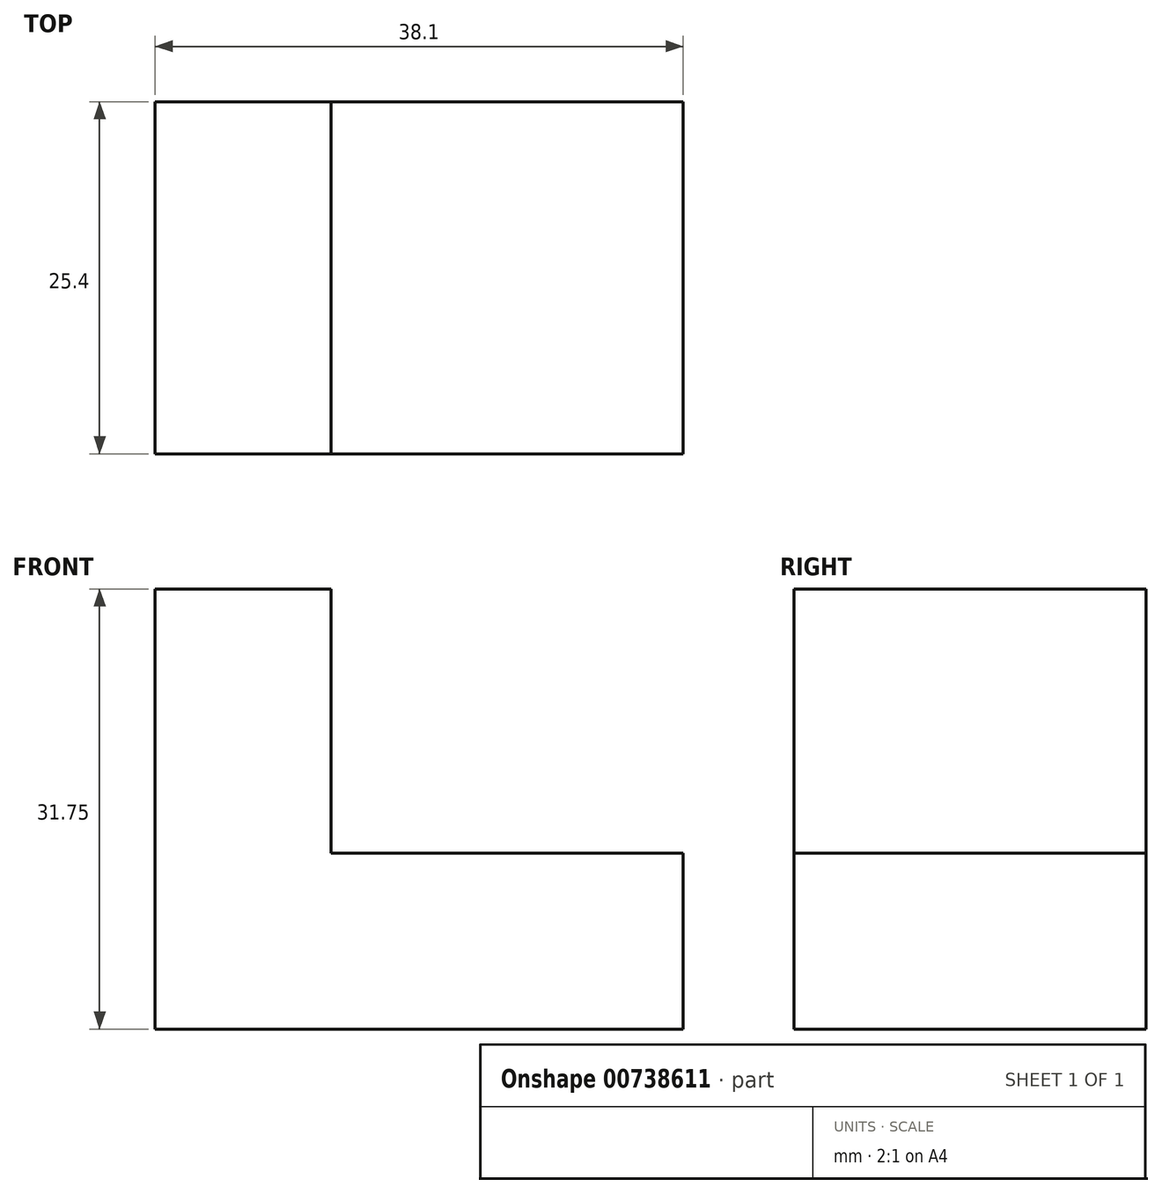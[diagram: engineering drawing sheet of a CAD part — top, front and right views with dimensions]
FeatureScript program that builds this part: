
annotation { "Feature Type Name" : "Feature", "Feature Type Description" : "" }
export const myFeature = defineFeature(function(context is Context, id is Id, definition is map)
    precondition{}
    {
        {
            var Q0;
            Q0=qCreatedBy(makeId("Front.planeOp"),FACE);
            var sketch = newSketch(context, id + "F0", { "sketchPlane" : qUnion([Q0])});
            skLineSegment(sketch, "E0", {"start": v(0, 31.75) * mm, "end": v(0, 0) * mm});
            skLineSegment(sketch, "E1", {"start": v(0, 0) * mm, "end": v(38.1, 0) * mm});
            skLineSegment(sketch, "E2", {"start": v(38.1, 0) * mm, "end": v(38.1, 12.7) * mm});
            skLineSegment(sketch, "E3", {"start": v(38.1, 12.7) * mm, "end": v(12.7, 12.7) * mm});
            skLineSegment(sketch, "E4", {"start": v(12.7, 12.7) * mm, "end": v(12.7, 31.75) * mm});
            skLineSegment(sketch, "E5", {"start": v(12.7, 31.75) * mm, "end": v(0, 31.75) * mm});
            skSolve(sketch);
        }
        {
            var Q0;
            Q0 = qSketchRegion(id + "F0", true);
            extrude(context, id + "F1", {"entities" : qUnion([Q0]), "depth" : 25.4 * mm, "offsetDistance" : 25.4 * mm});
        }
    });
